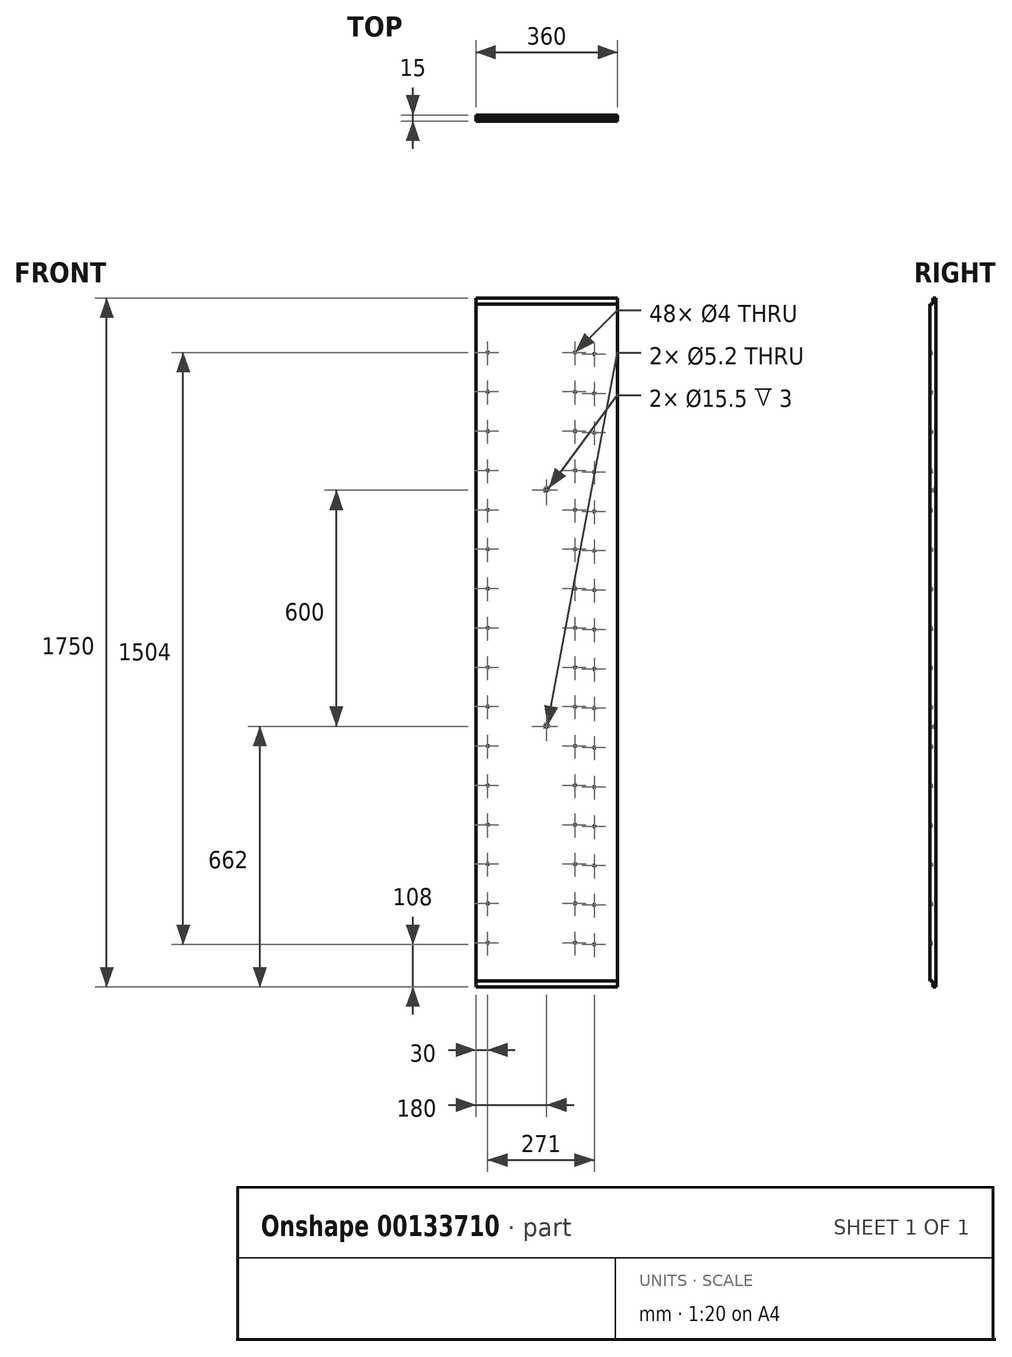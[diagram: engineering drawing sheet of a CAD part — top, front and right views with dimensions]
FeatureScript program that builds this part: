
annotation { "Feature Type Name" : "Feature", "Feature Type Description" : "" }
export const myFeature = defineFeature(function(context is Context, id is Id, definition is map)
    precondition{}
    {
        {
            var Q0;
            Q0=qCreatedBy(makeId("Front.planeOp"),FACE);
            var sketch = newSketch(context, id + "F0", { "sketchPlane" : qUnion([Q0])});
            skLineSegment(sketch, "E0.bottom", {"start": v(0, 0) * mm, "end": v(360, 0) * mm});
            skLineSegment(sketch, "E0.top", {"start": v(0, 1750) * mm, "end": v(360, 1750) * mm});
            skLineSegment(sketch, "E0.left", {"start": v(0, 0) * mm, "end": v(0, 1750) * mm});
            skLineSegment(sketch, "E0.right", {"start": v(360, 0) * mm, "end": v(360, 1750) * mm});
            skSolve(sketch);
        }
        {
            var Q0;
            Q0=makeQuery(id+"F0.imprint","IMPRINT",FACE,{"disambiguationData":[TD([[makeQuery(id+"F0.imprint","IMPRINT",EDGE,{"derivedFrom":sQuery(id+"F0.wireOp",EDGE,"E0.bottom")}),1.0]])]});
            extrude(context, id + "F1", {"entities" : qUnion([Q0]), "depth" : 15 * mm, "offsetDistance" : 25 * mm});
        }
        {
            var Q0;
            Q0=makeQuery(id+"F1.opExtrude","CAP_FACE",FACE,{"disambiguationData":[OSD([sQuery(id+"F0.wireOp",EDGE,"E0.bottom"),sQuery(id+"F0.wireOp",EDGE,"E0.top"),sQuery(id+"F0.wireOp",EDGE,"E0.left"),sQuery(id+"F0.wireOp",EDGE,"E0.right")])],"isStart":false});
            var sketch = newSketch(context, id + "F2", { "sketchPlane" : qUnion([Q0])});
            skPoint(sketch, "E1", {"position": v(252, 112) * mm});
            skPoint(sketch, "E2", {"position": v(30, 112) * mm});
            skPoint(sketch, "E3", {"position": v(301, 108) * mm});
            skPoint(sketch, "E4.0.1.0", {"position": v(30, 212) * mm});
            skPoint(sketch, "E4.0.1.1", {"position": v(252, 212) * mm});
            skPoint(sketch, "E4.0.1.2", {"position": v(301, 208) * mm});
            skPoint(sketch, "E4.0.2.0", {"position": v(30, 312) * mm});
            skPoint(sketch, "E4.0.2.1", {"position": v(252, 312) * mm});
            skPoint(sketch, "E4.0.2.2", {"position": v(301, 308) * mm});
            skPoint(sketch, "E4.0.3.0", {"position": v(30, 412) * mm});
            skPoint(sketch, "E4.0.3.1", {"position": v(252, 412) * mm});
            skPoint(sketch, "E4.0.3.2", {"position": v(301, 408) * mm});
            skPoint(sketch, "E4.0.4.0", {"position": v(30, 512) * mm});
            skPoint(sketch, "E4.0.4.1", {"position": v(252, 512) * mm});
            skPoint(sketch, "E4.0.4.2", {"position": v(301, 508) * mm});
            skPoint(sketch, "E4.0.5.0", {"position": v(30, 612) * mm});
            skPoint(sketch, "E4.0.5.1", {"position": v(252, 612) * mm});
            skPoint(sketch, "E4.0.5.2", {"position": v(301, 608) * mm});
            skPoint(sketch, "E4.0.6.0", {"position": v(30, 712) * mm});
            skPoint(sketch, "E4.0.6.1", {"position": v(252, 712) * mm});
            skPoint(sketch, "E4.0.6.2", {"position": v(301, 708) * mm});
            skPoint(sketch, "E4.0.7.0", {"position": v(30, 812) * mm});
            skPoint(sketch, "E4.0.7.1", {"position": v(252, 812) * mm});
            skPoint(sketch, "E4.0.7.2", {"position": v(301, 808) * mm});
            skPoint(sketch, "E4.0.8.0", {"position": v(30, 912) * mm});
            skPoint(sketch, "E4.0.8.1", {"position": v(252, 912) * mm});
            skPoint(sketch, "E4.0.8.2", {"position": v(301, 908) * mm});
            skPoint(sketch, "E4.0.9.0", {"position": v(30, 1012) * mm});
            skPoint(sketch, "E4.0.9.1", {"position": v(252, 1012) * mm});
            skPoint(sketch, "E4.0.9.2", {"position": v(301, 1008) * mm});
            skPoint(sketch, "E4.0.10.0", {"position": v(30, 1112) * mm});
            skPoint(sketch, "E4.0.10.1", {"position": v(252, 1112) * mm});
            skPoint(sketch, "E4.0.10.2", {"position": v(301, 1108) * mm});
            skPoint(sketch, "E4.0.11.0", {"position": v(30, 1212) * mm});
            skPoint(sketch, "E4.0.11.1", {"position": v(252, 1212) * mm});
            skPoint(sketch, "E4.0.11.2", {"position": v(301, 1208) * mm});
            skPoint(sketch, "E4.0.12.0", {"position": v(30, 1312) * mm});
            skPoint(sketch, "E4.0.12.1", {"position": v(252, 1312) * mm});
            skPoint(sketch, "E4.0.12.2", {"position": v(301, 1308) * mm});
            skPoint(sketch, "E4.0.13.0", {"position": v(30, 1412) * mm});
            skPoint(sketch, "E4.0.13.1", {"position": v(252, 1412) * mm});
            skPoint(sketch, "E4.0.13.2", {"position": v(301, 1408) * mm});
            skPoint(sketch, "E4.0.14.0", {"position": v(30, 1512) * mm});
            skPoint(sketch, "E4.0.14.1", {"position": v(252, 1512) * mm});
            skPoint(sketch, "E4.0.14.2", {"position": v(301, 1508) * mm});
            skPoint(sketch, "E4.0.15.0", {"position": v(30, 1612) * mm});
            skPoint(sketch, "E4.0.15.1", {"position": v(252, 1612) * mm});
            skPoint(sketch, "E4.0.15.2", {"position": v(301, 1608) * mm});
            skLineSegment(sketch, "E4.direction2", {"start": v(30, 112) * mm, "end": v(30, 212) * mm, "construction": true});
            skSolve(sketch);
        }
        {
            var Q0;
            Q0=sQuery(id+"F2.wireOp",VERTEX,"E4.0.15.1");
            var Q1;
            Q1=sQuery(id+"F2.wireOp",VERTEX,"E4.0.3.2");
            var Q2;
            Q2=sQuery(id+"F2.wireOp",VERTEX,"E4.0.4.2");
            var Q3;
            Q3=sQuery(id+"F2.wireOp",VERTEX,"E4.0.3.1");
            var Q4;
            Q4=sQuery(id+"F2.wireOp",VERTEX,"E4.0.10.2");
            var Q5;
            Q5=sQuery(id+"F2.wireOp",VERTEX,"E4.0.8.1");
            var Q6;
            Q6=sQuery(id+"F2.wireOp",VERTEX,"E4.0.13.2");
            var Q7;
            Q7=sQuery(id+"F2.wireOp",VERTEX,"E4.0.3.0");
            var Q8;
            Q8=sQuery(id+"F2.wireOp",VERTEX,"E4.0.5.1");
            var Q9;
            Q9=sQuery(id+"F2.wireOp",VERTEX,"E4.0.11.1");
            var Q10;
            Q10=sQuery(id+"F2.wireOp",VERTEX,"E4.0.9.0");
            var Q11;
            Q11=sQuery(id+"F2.wireOp",VERTEX,"E4.0.14.1");
            var Q12;
            Q12=sQuery(id+"F2.wireOp",VERTEX,"E4.0.2.0");
            var Q13;
            Q13=sQuery(id+"F2.wireOp",VERTEX,"E4.0.2.1");
            var Q14;
            Q14=sQuery(id+"F2.wireOp",VERTEX,"E4.0.2.2");
            var Q15;
            Q15=sQuery(id+"F2.wireOp",VERTEX,"E4.0.7.0");
            var Q16;
            Q16=sQuery(id+"F2.wireOp",VERTEX,"E4.0.12.0");
            var Q17;
            Q17=sQuery(id+"F2.wireOp",VERTEX,"E4.0.15.2");
            var Q18;
            Q18=sQuery(id+"F2.wireOp",VERTEX,"E4.0.10.1");
            var Q19;
            Q19=sQuery(id+"F2.wireOp",VERTEX,"E4.0.9.2");
            var Q20;
            Q20=sQuery(id+"F2.wireOp",VERTEX,"E4.0.15.0");
            var Q21;
            Q21=sQuery(id+"F2.wireOp",VERTEX,"E4.0.6.0");
            var Q22;
            Q22=sQuery(id+"F2.wireOp",VERTEX,"E4.0.8.2");
            var Q23;
            Q23=sQuery(id+"F2.wireOp",VERTEX,"E3");
            var Q24;
            Q24=sQuery(id+"F2.wireOp",VERTEX,"E4.direction1.end");
            var Q25;
            Q25=sQuery(id+"F2.wireOp",VERTEX,"E4.0.4.0");
            var Q26;
            Q26=sQuery(id+"F2.wireOp",VERTEX,"E4.0.10.0");
            var Q27;
            Q27=sQuery(id+"F2.wireOp",VERTEX,"E4.0.6.1");
            var Q28;
            Q28=sQuery(id+"F2.wireOp",VERTEX,"E4.0.11.0");
            var Q29;
            Q29=sQuery(id+"F2.wireOp",VERTEX,"E4.direction2.end");
            var Q30;
            Q30=sQuery(id+"F2.wireOp",VERTEX,"E4.0.12.2");
            var Q31;
            Q31=sQuery(id+"F2.wireOp",VERTEX,"E4.0.13.1");
            var Q32;
            Q32=sQuery(id+"F2.wireOp",VERTEX,"E4.0.12.1");
            var Q33;
            Q33=sQuery(id+"F2.wireOp",VERTEX,"E4.0.5.2");
            var Q34;
            Q34=sQuery(id+"F2.wireOp",VERTEX,"E4.0.14.0");
            var Q35;
            Q35=sQuery(id+"F2.wireOp",VERTEX,"E4.0.7.2");
            var Q36;
            Q36=sQuery(id+"F2.wireOp",VERTEX,"E4.direction2.start");
            var Q37;
            Q37=sQuery(id+"F2.wireOp",VERTEX,"E4.0.6.2");
            var Q38;
            Q38=sQuery(id+"F2.wireOp",VERTEX,"E4.0.5.0");
            var Q39;
            Q39=sQuery(id+"F2.wireOp",VERTEX,"E4.0.4.1");
            var Q40;
            Q40=sQuery(id+"F2.wireOp",VERTEX,"E4.0.9.1");
            var Q41;
            Q41=sQuery(id+"F2.wireOp",VERTEX,"E1");
            var Q42;
            Q42=sQuery(id+"F2.wireOp",VERTEX,"E4.0.11.2");
            var Q43;
            Q43=sQuery(id+"F2.wireOp",VERTEX,"E4.0.13.0");
            var Q44;
            Q44=sQuery(id+"F2.wireOp",VERTEX,"E4.0.8.0");
            var Q45;
            Q45=sQuery(id+"F2.wireOp",VERTEX,"E4.0.1.2");
            var Q46;
            Q46=sQuery(id+"F2.wireOp",VERTEX,"E4.0.7.1");
            var Q47;
            Q47=sQuery(id+"F2.wireOp",VERTEX,"E4.0.14.2");
            var Q48;
            Q48=sQuery(id+"F2.wireOp",VERTEX,"E4.0.1.1");
            var Q49;
            Q49=makeQuery(id+"F1.opExtrude","SWEPT_BODY",BODY,{"disambiguationData":[OSD([sQuery(id+"F0.wireOp",EDGE,"E0.bottom"),sQuery(id+"F0.wireOp",EDGE,"E0.top"),sQuery(id+"F0.wireOp",EDGE,"E0.left"),sQuery(id+"F0.wireOp",EDGE,"E0.right")])]});
            hole(context, id + "F3", {"style" : HoleStyle.SIMPLE, "endStyle" : HoleEndStyle.BLIND, "holeDiameter" : 4 * mm, "holeDepth" : 5 * mm, "isTappedThrough" : true, "tappedDepth" : 12 * mm, "tapClearance" : 3, "startFromSketch" : true, "locations" : qUnion([Q0, Q1, Q2, Q3, Q4, Q5, Q6, Q7, Q8, Q9, Q10, Q11, Q12, Q13, Q14, Q15, Q16, Q17, Q18, Q19, Q20, Q21, Q22, Q23, Q24, Q25, Q26, Q27, Q28, Q29, Q30, Q31, Q32, Q33, Q34, Q35, Q36, Q37, Q38, Q39, Q40, Q41, Q42, Q43, Q44, Q45, Q46, Q47, Q48]), "scope" : qUnion([Q49])});
        }
        {
            var Q0;
            Q0=makeQuery(id+"F1.opExtrude","CAP_FACE",FACE,{"disambiguationData":[OSD([sQuery(id+"F0.wireOp",EDGE,"E0.bottom"),sQuery(id+"F0.wireOp",EDGE,"E0.top"),sQuery(id+"F0.wireOp",EDGE,"E0.left"),sQuery(id+"F0.wireOp",EDGE,"E0.right")])],"isStart":true});
            var sketch = newSketch(context, id + "F4", { "sketchPlane" : qUnion([Q0])});
            skPoint(sketch, "E5.positionSnap0", {"position": v(-180, 0) * mm});
            skPoint(sketch, "E6", {"position": v(-180, 662) * mm});
            skPoint(sketch, "E7", {"position": v(-180, 1262) * mm});
            skSolve(sketch);
        }
        {
            var Q0;
            Q0=sQuery(id+"F4.wireOp",VERTEX,"E7");
            var Q1;
            Q1=sQuery(id+"F4.wireOp",VERTEX,"E6");
            var Q2;
            Q2=makeQuery(id+"F1.opExtrude","SWEPT_BODY",BODY,{"disambiguationData":[OSD([sQuery(id+"F0.wireOp",EDGE,"E0.bottom"),sQuery(id+"F0.wireOp",EDGE,"E0.top"),sQuery(id+"F0.wireOp",EDGE,"E0.left"),sQuery(id+"F0.wireOp",EDGE,"E0.right")])]});
            hole(context, id + "F5", {"style" : HoleStyle.C_BORE, "endStyle" : HoleEndStyle.BLIND, "holeDiameter" : 5.2 * mm, "cBoreDiameter" : 15.5 * mm, "cBoreDepth" : 3 * mm, "holeDepth" : 15 * mm, "isTappedThrough" : true, "tappedDepth" : 12 * mm, "tapClearance" : 3, "startFromSketch" : true, "locations" : qUnion([Q0, Q1]), "scope" : qUnion([Q2])});
        }
        {
            var Q0;
            Q0=makeQuery(id+"F1.opExtrude","SWEPT_FACE",FACE,{"disambiguationData":[OSD([sQuery(id+"F0.wireOp",EDGE,"E0.left")])]});
            var sketch = newSketch(context, id + "F6", { "sketchPlane" : qUnion([Q0])});
            skSolve(sketch);
        }
        {
            var Q0;
            {var subQ0=sQuery(id+"F0.wireOp",EDGE,"E0.left");Q0=makeQuery(id+"F6.imprint","IMPRINT",FACE,{"disambiguationData":[TD([[makeQuery(id+"F6.imprint","IMPRINT",EDGE,{"derivedFrom":makeQuery(id+"F1.opExtrude","CAP_EDGE",EDGE,{"disambiguationData":[OSD([subQ0])],"isStart":true})}),-1.0]])]});}
            var sketch = newSketch(context, id + "F7", { "sketchPlane" : qUnion([Q0])});
            skPoint(sketch, "E8.0", {"position": v(15, 1750) * mm});
            skLineSegment(sketch, "E9.bottom", {"start": v(15, 1750) * mm, "end": v(7.5, 1750) * mm});
            skLineSegment(sketch, "E9.top", {"start": v(15, 1735) * mm, "end": v(7.5, 1735) * mm});
            skLineSegment(sketch, "E9.left", {"start": v(15, 1750) * mm, "end": v(15, 1735) * mm});
            skLineSegment(sketch, "E9.right", {"start": v(7.5, 1750) * mm, "end": v(7.5, 1735) * mm});
            skPoint(sketch, "E10.0", {"position": v(15, 0) * mm});
            skLineSegment(sketch, "E11.bottom", {"start": v(15, 0) * mm, "end": v(7.5, 0) * mm});
            skLineSegment(sketch, "E11.top", {"start": v(15, 15) * mm, "end": v(7.5, 15) * mm});
            skLineSegment(sketch, "E11.left", {"start": v(15, 0) * mm, "end": v(15, 15) * mm});
            skLineSegment(sketch, "E11.right", {"start": v(7.5, 0) * mm, "end": v(7.5, 15) * mm});
            skSolve(sketch);
        }
        {
            var Q0;
            Q0 = qSketchRegion(id + "F7", true);
            extrude(context, id + "F8", {"entities" : qUnion([Q0]), "operationType" : NewBodyOperationType.REMOVE, "endBound" : BoundingType.UP_TO_NEXT, "oppositeDirection" : true, "depth" : 25 * mm, "offsetDistance" : 25 * mm});
        }
    });
